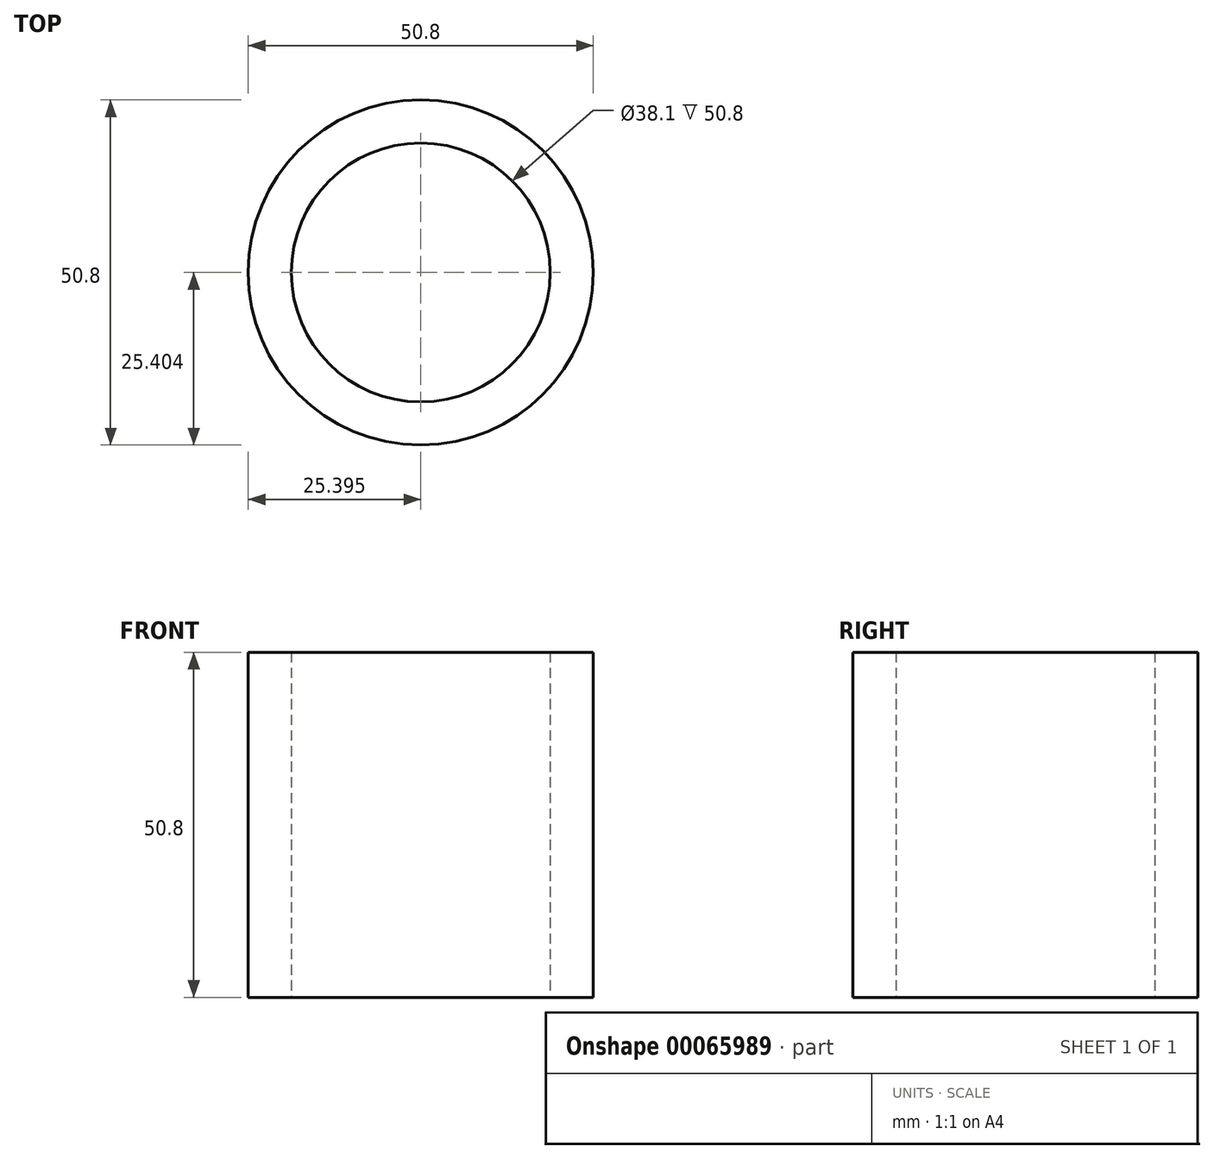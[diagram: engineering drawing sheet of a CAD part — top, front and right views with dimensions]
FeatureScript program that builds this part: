
annotation { "Feature Type Name" : "Feature", "Feature Type Description" : "" }
export const myFeature = defineFeature(function(context is Context, id is Id, definition is map)
    precondition{}
    {
        {
            var Q0;
            Q0=qCreatedBy(makeId("Top.planeOp"),FACE);
            var sketch = newSketch(context, id + "F0", { "sketchPlane" : qUnion([Q0])});
            skCircle(sketch, "E0", {"center": v(0, -0.12) * mm, "radius": 19.05 * mm});
            skCircle(sketch, "E1", {"center": v(0, -0.12) * mm, "radius": 25.4 * mm});
            skSolve(sketch);
        }
        {
            var Q0;
            Q0=sQuery(id+"F0.wireOp",EDGE,"E0");
            extrude(context, id + "F1", {"bodyType" : ToolBodyType.SURFACE, "surfaceEntities" : qUnion([Q0]), "depth" : 101.6 * mm});
        }
        {
            var Q0;
            Q0 = qSketchRegion(id + "F0", true);
            extrude(context, id + "F2", {"entities" : qUnion([Q0]), "depth" : 50.8 * mm});
        }
    });
